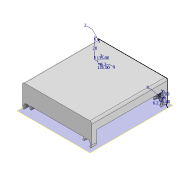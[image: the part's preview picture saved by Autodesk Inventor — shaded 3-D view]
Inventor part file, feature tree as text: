
AUTODESK INVENTOR PART (.ipt)
format: ipt  version: 2021 (Build 250183000, 183)  size: 190,976 bytes
history: native  units: mm
features: extrude x5, sketch x4, fillet x1, plane x1
ambient origin geometry x8: Origin, YZ Plane, XZ Plane, XY Plane, X Axis, Y Axis, Z Axis, Center Point
bodies: Solid1 (feature_tree)
feature tree (11):
  sketch  "Sketch1"  dims[d0=6.2mm d1=6.2mm d2=9.0mm]
  extrude  "Extrusion1"  Depth=9.0mm
  fillet  "Fillet1"  Radius=9.0mm
  extrude  "Extrusion3"  TaperAngle=135.0deg  [1 undecoded]
  plane  "Work Plane1"
  extrude  "Extrusion2"  Depth=20.0mm
  extrude  "Extrusion4"  Depth=2.0mm
  extrude  "Extrusion5"  Depth=2.0mm
  sketch  "Sketch2"  dims[d3=9.0mm d4=135.0deg]
  sketch  "Sketch3"  dims[d5=45.0deg d6=20.0mm]
  sketch  "Sketch4"  dims[d8=75.0mm d9=0.0mm d10=2.0mm d11=22.0mm d12=80.0mm d13=65.0mm d14=37.5mm d15=15.0mm d16=0.0mm d17=135.0deg d18=3.0mm d19=45.0deg d20=3.0mm d21=75.0mm d22=0.0mm d23=2.0mm d24=2.0mm d25=2.0mm d26=0.0mm d27=2.0mm d28=2.0mm d29=0.0mm d30=0.5mm d31=0.872665mm]
note: 1 required parameter value undecoded (feature->parameter linkage not recoverable at this tier; creation-order binding heuristic only, values carry confidence <= 0.55)
